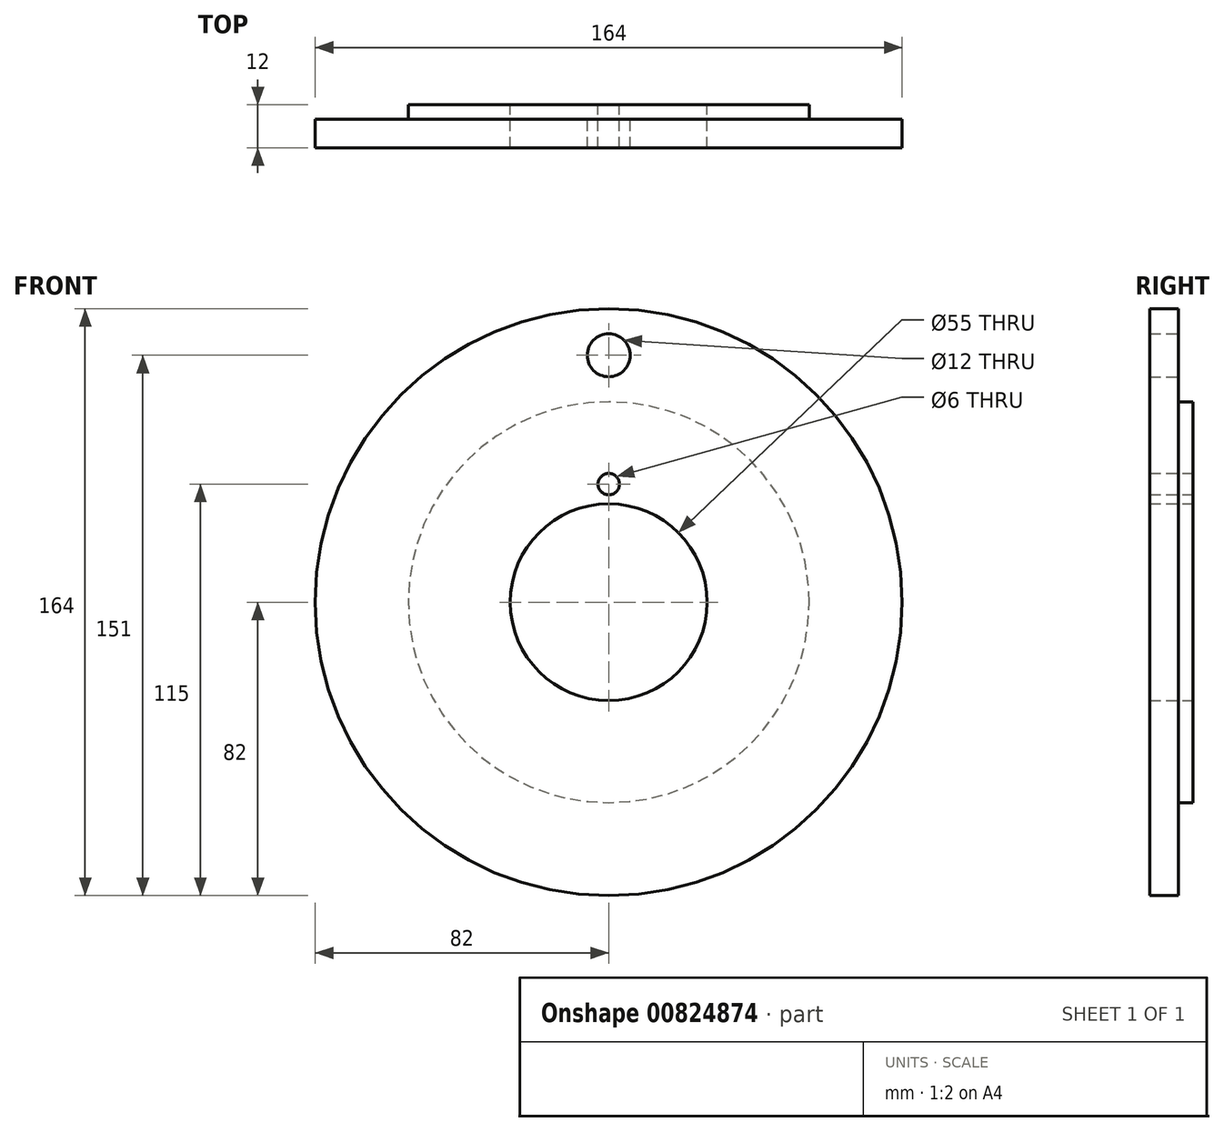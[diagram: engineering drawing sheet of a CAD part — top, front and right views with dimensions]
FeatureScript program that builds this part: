
annotation { "Feature Type Name" : "Feature", "Feature Type Description" : "" }
export const myFeature = defineFeature(function(context is Context, id is Id, definition is map)
    precondition{}
    {
        {
            var Q0;
            Q0=qCreatedBy(makeId("Front.planeOp"),FACE);
            var sketch = newSketch(context, id + "F0", { "sketchPlane" : qUnion([Q0])});
            skCircle(sketch, "E0", {"center": v(0, 0) * mm, "radius": 82 * mm});
            skCircle(sketch, "E1", {"center": v(0, 0) * mm, "radius": 27.5 * mm});
            skCircle(sketch, "E2", {"center": v(0, 0) * mm, "radius": 56 * mm});
            skCircle(sketch, "E3", {"center": v(0, 0) * mm, "radius": 69 * mm, "construction": true});
            skCircle(sketch, "E4", {"center": v(0, 0) * mm, "radius": 33 * mm, "construction": true});
            skCircle(sketch, "E5", {"center": v(0, 33) * mm, "radius": 3 * mm});
            skCircle(sketch, "E6", {"center": v(0, 69) * mm, "radius": 6 * mm});
            skSolve(sketch);
        }
        {
            var Q0;
            Q0=makeQuery(id+"F0.imprint","IMPRINT",FACE,{"disambiguationData":[TD([[makeQuery(id+"F0.imprint","IMPRINT",EDGE,{"derivedFrom":sQuery(id+"F0.wireOp",EDGE,"E1")}),-1.0]])]});
            var Q1;
            Q1=makeQuery(id+"F0.imprint","IMPRINT",FACE,{"disambiguationData":[TD([[makeQuery(id+"F0.imprint","IMPRINT",EDGE,{"derivedFrom":sQuery(id+"F0.wireOp",EDGE,"E0")}),1.0]])]});
            var Q2;
            Q2=makeQuery(id+"F0.imprint","IMPRINT",FACE,{"disambiguationData":[TD([[makeQuery(id+"F0.imprint","IMPRINT",EDGE,{"derivedFrom":sQuery(id+"F0.wireOp",EDGE,"E5")}),1.0]])]});
            var Q3;
            Q3=makeQuery(id+"F0.imprint","IMPRINT",FACE,{"disambiguationData":[TD([[makeQuery(id+"F0.imprint","IMPRINT",EDGE,{"derivedFrom":sQuery(id+"F0.wireOp",EDGE,"E6")}),1.0]])]});
            extrude(context, id + "F1", {"entities" : qUnion([Q0, Q1, Q2, Q3]), "depth" : 8 * mm, "offsetDistance" : 25.4 * mm});
        }
        {
            var Q0;
            Q0=makeQuery(id+"F0.imprint","IMPRINT",FACE,{"disambiguationData":[TD([[makeQuery(id+"F0.imprint","IMPRINT",EDGE,{"derivedFrom":sQuery(id+"F0.wireOp",EDGE,"E1")}),-1.0]])]});
            var Q1;
            Q1=makeQuery(id+"F0.imprint","IMPRINT",FACE,{"disambiguationData":[TD([[makeQuery(id+"F0.imprint","IMPRINT",EDGE,{"derivedFrom":sQuery(id+"F0.wireOp",EDGE,"E5")}),1.0]])]});
            extrude(context, id + "F2", {"entities" : qUnion([Q0, Q1]), "operationType" : NewBodyOperationType.ADD, "oppositeDirection" : true, "depth" : 4 * mm, "offsetDistance" : 25.4 * mm});
        }
        {
            var Q0;
            Q0=makeQuery(id+"F0.imprint","IMPRINT",FACE,{"disambiguationData":[TD([[makeQuery(id+"F0.imprint","IMPRINT",EDGE,{"derivedFrom":sQuery(id+"F0.wireOp",EDGE,"E6")}),1.0]])]});
            extrude(context, id + "F3", {"entities" : qUnion([Q0]), "operationType" : NewBodyOperationType.REMOVE, "depth" : 8 * mm, "offsetDistance" : 25.4 * mm});
        }
        {
            var Q0;
            Q0=makeQuery(id+"F2.opExtrude","CAP_FACE",FACE,{"disambiguationData":[OSD([sQuery(id+"F0.wireOp",EDGE,"E1"),sQuery(id+"F0.wireOp",EDGE,"E2")])],"isStart":false});
            var sketch = newSketch(context, id + "F4", { "sketchPlane" : qUnion([Q0])});
            skCircle(sketch, "E7", {"center": v(0, 33) * mm, "radius": 3 * mm});
            skSolve(sketch);
        }
        {
            var Q0;
            Q0 = qSketchRegion(id + "F4", true);
            extrude(context, id + "F5", {"entities" : qUnion([Q0]), "operationType" : NewBodyOperationType.REMOVE, "oppositeDirection" : true, "depth" : 12 * mm, "offsetDistance" : 25.4 * mm});
        }
    });
